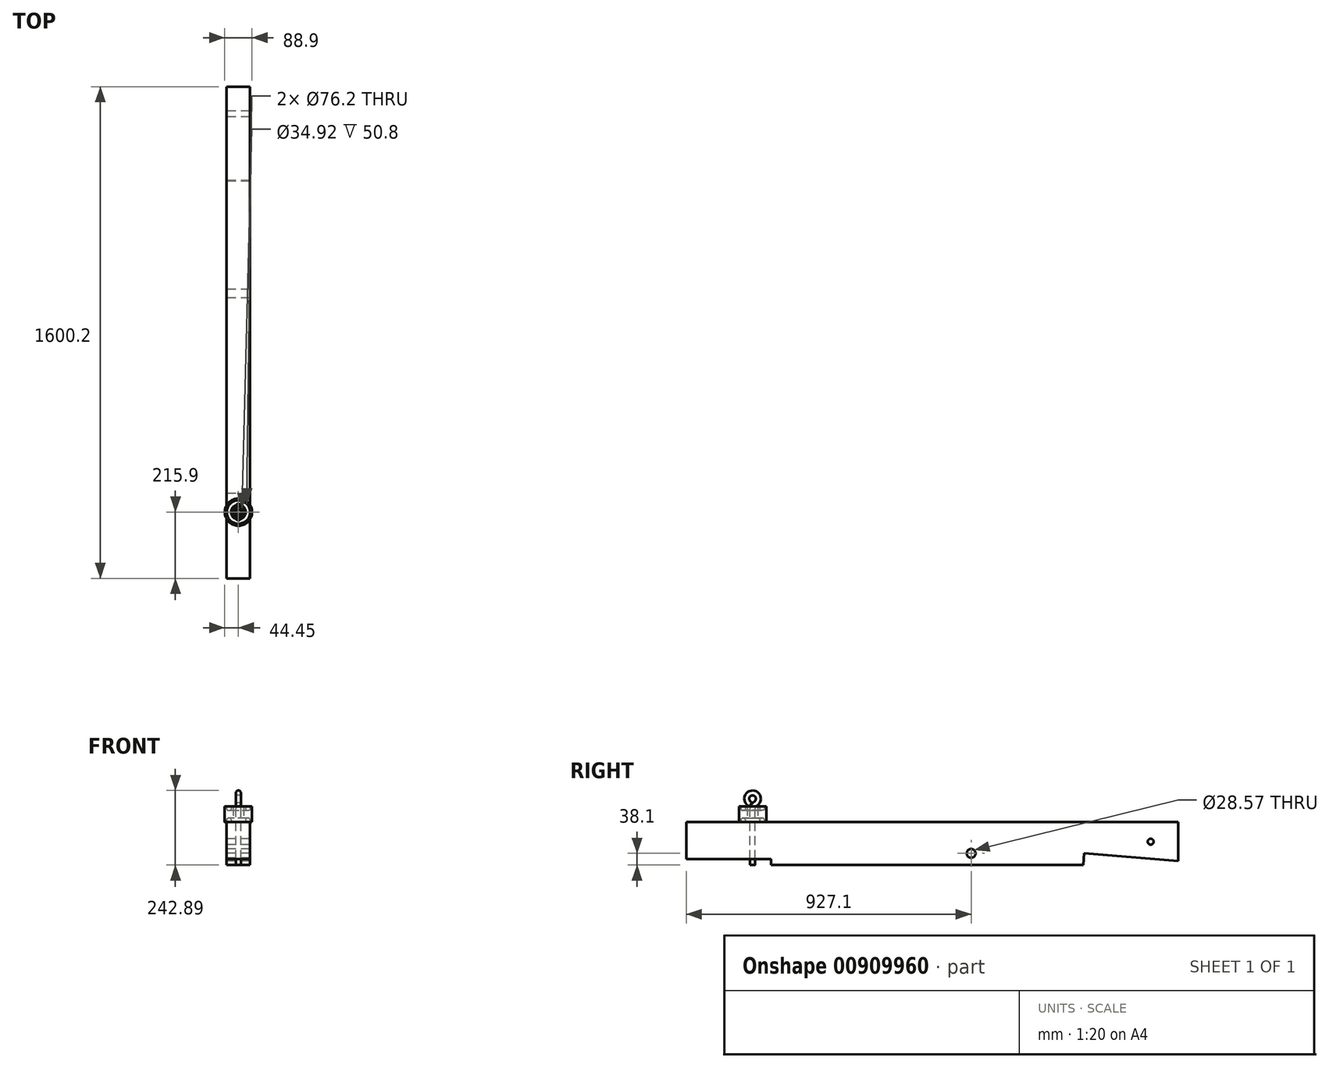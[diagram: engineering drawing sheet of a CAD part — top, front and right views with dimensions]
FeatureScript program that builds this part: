
annotation { "Feature Type Name" : "Feature", "Feature Type Description" : "" }
export const myFeature = defineFeature(function(context is Context, id is Id, definition is map)
    precondition{}
    {
        {
            var Q0;
            Q0=qCreatedBy(makeId("Right.planeOp"),FACE);
            var sketch = newSketch(context, id + "F0", { "sketchPlane" : qUnion([Q0])});
            skLineSegment(sketch, "E0", {"start": v(492.12, -69.85) * mm, "end": v(-523.54, -69.85) * mm});
            skLineSegment(sketch, "E1", {"start": v(-523.54, -69.85) * mm, "end": v(-523.54, -50.8) * mm});
            skLineSegment(sketch, "E2", {"start": v(-523.54, -50.8) * mm, "end": v(-800.1, -50.8) * mm});
            skLineSegment(sketch, "E3", {"start": v(-800.1, -50.8) * mm, "end": v(-800.1, 69.85) * mm});
            skLineSegment(sketch, "E4", {"start": v(-800.1, 69.85) * mm, "end": v(800.1, 69.85) * mm});
            skLineSegment(sketch, "E5", {"start": v(800.1, 69.85) * mm, "end": v(800.1, -57.15) * mm});
            skCircle(sketch, "E6", {"center": v(711.2, 6.35) * mm, "radius": 9.53 * mm});
            skCircle(sketch, "E7", {"center": v(127, -31.75) * mm, "radius": 14.29 * mm});
            skLineSegment(sketch, "E8", {"start": v(492.12, -69.85) * mm, "end": v(495.3, -31.75) * mm});
            skLineSegment(sketch, "E9", {"start": v(495.3, -31.75) * mm, "end": v(800.1, -57.15) * mm});
            skLineSegment(sketch, "E10", {"start": v(0, 69.85) * mm, "end": v(0, 0) * mm, "construction": true});
            skLineSegment(sketch, "E11", {"start": v(0, -69.85) * mm, "end": v(0, 0) * mm, "construction": true});
            skSolve(sketch);
        }
        {
            var Q0;
            Q0=makeQuery(id+"F0.imprint","IMPRINT",FACE,{"disambiguationData":[TD([[makeQuery(id+"F0.imprint","IMPRINT",EDGE,{"derivedFrom":sQuery(id+"F0.wireOp",EDGE,"E0")}),-1.0]])]});
            extrude(context, id + "F1", {"entities" : qUnion([Q0]), "depth" : 76.2 * mm, "offsetDistance" : 25 * mm, "symmetric" : true});
        }
        {
            var Q0;
            Q0=makeQuery(id+"F1.opExtrude","SWEPT_FACE",FACE,{"disambiguationData":[OSD([sQuery(id+"F0.wireOp",EDGE,"E4")])]});
            var sketch = newSketch(context, id + "F2", { "sketchPlane" : qUnion([Q0])});
            skCircle(sketch, "E12", {"center": v(0, -584.2) * mm, "radius": 7.94 * mm});
            skSolve(sketch);
        }
        {
            var Q0;
            Q0=makeQuery(id+"F2.imprint","IMPRINT",FACE,{"disambiguationData":[TD([[makeQuery(id+"F2.imprint","IMPRINT",EDGE,{"derivedFrom":sQuery(id+"F2.wireOp",EDGE,"E12")}),1.0]])]});
            extrude(context, id + "F3", {"entities" : qUnion([Q0]), "operationType" : NewBodyOperationType.REMOVE, "endBound" : BoundingType.THROUGH_ALL, "oppositeDirection" : true, "depth" : 25 * mm, "offsetDistance" : 25 * mm});
        }
        {
            var Q0;
            Q0=qCreatedBy(makeId("Right.planeOp"),FACE);
            var sketch = newSketch(context, id + "F4", { "sketchPlane" : qUnion([Q0])});
            skLineSegment(sketch, "E13", {"start": v(-584.2, -69.85) * mm, "end": v(-584.2, 113.05) * mm});
            skArc(sketch, "E14", {"start": v(-574.68, 129.55) * mm, "mid": v(-584.2, 165.1) * mm, "end": v(-593.73, 129.55) * mm});
            skArc(sketch, "E15", {"start": v(-574.68, 129.55) * mm, "mid": v(-581.65, 122.58) * mm, "end": v(-584.2, 113.05) * mm});
            skPoint(sketch, "E16.orphan", {"position": v(-584.2, 129.55) * mm});
            skLineSegment(sketch, "E17", {"start": v(-593.73, 129.55) * mm, "end": v(-590.3, 127.58) * mm});
            skLineSegment(sketch, "E18", {"start": v(-566.74, 69.85) * mm, "end": v(-566.74, 120.65) * mm});
            skLineSegment(sketch, "E19", {"start": v(-566.74, 120.65) * mm, "end": v(-560.39, 120.65) * mm});
            skLineSegment(sketch, "E20", {"start": v(-560.39, 120.65) * mm, "end": v(-560.39, 107.95) * mm});
            skLineSegment(sketch, "E21", {"start": v(-560.39, 107.95) * mm, "end": v(-546.1, 107.95) * mm});
            skLineSegment(sketch, "E22", {"start": v(-546.1, 107.95) * mm, "end": v(-546.1, 120.65) * mm});
            skLineSegment(sketch, "E23", {"start": v(-546.1, 120.65) * mm, "end": v(-539.75, 120.65) * mm});
            skLineSegment(sketch, "E24", {"start": v(-539.75, 120.65) * mm, "end": v(-539.75, 69.85) * mm});
            skLineSegment(sketch, "E25", {"start": v(-539.75, 69.85) * mm, "end": v(-546.1, 69.85) * mm});
            skLineSegment(sketch, "E26", {"start": v(-546.1, 69.85) * mm, "end": v(-546.1, 82.55) * mm});
            skLineSegment(sketch, "E27", {"start": v(-546.1, 82.55) * mm, "end": v(-560.39, 82.55) * mm});
            skLineSegment(sketch, "E28", {"start": v(-560.39, 82.55) * mm, "end": v(-560.39, 69.85) * mm});
            skLineSegment(sketch, "E29", {"start": v(-560.39, 69.85) * mm, "end": v(-566.74, 69.85) * mm});
            skSolve(sketch);
        }
        {
            var Q0;
            Q0=sQuery(id+"F4.wireOp",VERTEX,"E13.start");
            var Q1;
            Q1=sQuery(id+"F4.wireOp",EDGE,"E13");
            cPlane(context, id + "F5", {"entities" : qUnion([Q0, Q1]), "cplaneType" : CPlaneType.LINE_POINT, "offset" : 25 * mm, "width" : 150 * mm, "height" : 150 * mm});
        }
        {
            var Q0;
            Q0=qCreatedBy(id+"F5.planeOp",FACE);
            var sketch = newSketch(context, id + "F6", { "sketchPlane" : qUnion([Q0])});
            skCircle(sketch, "E30", {"center": v(0, -584.2) * mm, "radius": 7.94 * mm});
            skSolve(sketch);
        }
        {
            var Q0;
            Q0=makeQuery(id+"F6.imprint","IMPRINT",FACE,{"disambiguationData":[TD([[makeQuery(id+"F6.imprint","IMPRINT",EDGE,{"derivedFrom":sQuery(id+"F6.wireOp",EDGE,"E30")}),1.0]])]});
            var Q1;
            Q1=sQuery(id+"F4.wireOp",EDGE,"E13");
            var Q2;
            Q2=sQuery(id+"F4.wireOp",EDGE,"E15");
            var Q3;
            Q3=sQuery(id+"F4.wireOp",EDGE,"E14");
            var Q4;
            Q4=sQuery(id+"F4.wireOp",EDGE,"E17");
            sweep(context, id + "F7", {"profiles" : qUnion([Q0]), "path" : qUnion([Q1, Q2, Q3, Q4])});
        }
        {
            var Q0;
            Q0=makeQuery(id+"F4.imprint","IMPRINT",FACE,{"disambiguationData":[TD([[makeQuery(id+"F4.imprint","IMPRINT",EDGE,{"derivedFrom":sQuery(id+"F4.wireOp",EDGE,"E18")}),-1.0]])]});
            var Q1;
            Q1=sQuery(id+"F4.wireOp",EDGE,"E13");
            revolve(context, id + "F8", {"surfaceOperationType" : NewSurfaceOperationType.NEW, "entities" : qUnion([Q0]), "axis" : qUnion([Q1]), "revolveType" : RevolveType.FULL});
        }
        {
            var Q0;
            Q0=makeQuery(id+"F8.opRevolve","SWEPT_EDGE",EDGE,{"disambiguationData":[OSD([sQuery(id+"F4.wireOp",EDGE,"E26"),sQuery(id+"F4.wireOp",EDGE,"E27")])]});
            var Q1;
            Q1=makeQuery(id+"F8.opRevolve","SWEPT_EDGE",EDGE,{"disambiguationData":[OSD([sQuery(id+"F4.wireOp",EDGE,"E27"),sQuery(id+"F4.wireOp",EDGE,"E28")])]});
            var Q2;
            Q2=makeQuery(id+"F8.opRevolve","SWEPT_FACE",FACE,{"disambiguationData":[OSD([sQuery(id+"F4.wireOp",EDGE,"E21")])]});
            fillet(context, id + "F9", {"entities" : qUnion([Q0, Q1, Q2]), "radius" : 4.76 * mm, "tangentPropagation" : true, "allowEdgeOverflow" : false});
        }
        {
            var Q0;
            Q0=makeQuery(id+"F8.opRevolve","SWEPT_EDGE",EDGE,{"disambiguationData":[OSD([sQuery(id+"F4.wireOp",EDGE,"E22"),sQuery(id+"F4.wireOp",EDGE,"E23")])]});
            var Q1;
            Q1=makeQuery(id+"F8.opRevolve","SWEPT_EDGE",EDGE,{"disambiguationData":[OSD([sQuery(id+"F4.wireOp",EDGE,"E25"),sQuery(id+"F4.wireOp",EDGE,"E26")])]});
            var Q2;
            Q2=makeQuery(id+"F8.opRevolve","SWEPT_EDGE",EDGE,{"disambiguationData":[OSD([sQuery(id+"F4.wireOp",EDGE,"E28"),sQuery(id+"F4.wireOp",EDGE,"E29")])]});
            var Q3;
            Q3=makeQuery(id+"F8.opRevolve","SWEPT_EDGE",EDGE,{"disambiguationData":[OSD([sQuery(id+"F4.wireOp",EDGE,"E19"),sQuery(id+"F4.wireOp",EDGE,"E20")])]});
            fillet(context, id + "F10", {"entities" : qUnion([Q0, Q1, Q2, Q3]), "radius" : 3.17 * mm, "tangentPropagation" : true, "allowEdgeOverflow" : false});
        }
    });
